# Revit family: 23-DESAGUE PUSH PLAST CON REBOSE
name_source: partatom
category: Aparatos sanitarios
revit_build: Autodesk Revit 2018 (Build: 20170223_1515(x64)
units: mm (PartAtom-declared; Revit-internal decimal feet)

## family parameters
Anfitrión = Cara
Compartido = No
Corte con vacíos al cargar = No
Cota de conector redondo = Diámetro de uso
Número OmniClass = 23.45.55.21
Punto de cálculo de habitación = No
Tipo de pieza = Normal
Título OmniClass = Drains (Wastes)

## types (1)
- 23-DESAGUE PUSH PLAST CON REBOSE
    Acabado = Brillante
    Altura Nominal = 345
    Ancho Nominal = 31
    Características = Permite drenar rápidamente el agua. fácil instalación y mantenimiento, resistente a la corrosión
    Color = Cromo
    Código de montaje = D2010
    Descripción = Plumbing Fixtures
    Descripción IFC = Desagüe largo plástico con rebose
    Diámetro de conexión Sanitaria = 0 mm  [stored 0 ft]
    Elevación por defecto = 0 mm  [stored 0 ft]
    Fabricante = www.corona.com.co
    Forma = Cilíndrica
    Información del producto = https://www.grival.com
    Logitud Nominal = 55
    Material Acabado = Cromo-Corona
    Material de Fabricación = Plástico
    Nombre = Desagüe largo con rebose
    Nombre del Fabricante = Corona
    Número Modelo = 935415551
    Requerimientos Accesibilidad = Manual
    Responsable Garantías Partes = www.corona.com.co
    Tamaño = 55 x 31 x 345
    Tipo de Activo = Fijo
    Tráfico = Residencial

note: [stored X ft] marks values corroborated as IEEE doubles in the binary element streams (Revit-internal decimal feet)

## geometry (parser evidence)
native form markers: Sweep x2
no freeform markers — native parametric forms only
